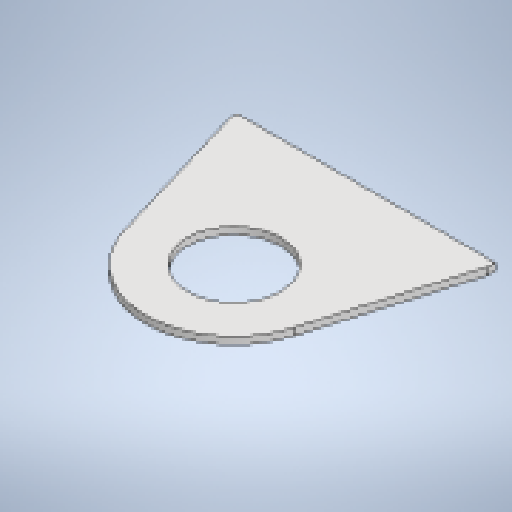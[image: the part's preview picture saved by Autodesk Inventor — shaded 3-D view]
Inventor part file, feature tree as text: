
AUTODESK INVENTOR PART (.ipt)
format: ipt  version: 2025.1 (Build 291241020, 241B)  size: 181,248 bytes
history: native  units: mm
features: other x2, sheet_metal_op x1, sketch x1
ambient origin geometry x8: Origin, YZ Plane, XZ Plane, XY Plane, X Axis, Y Axis, Z Axis, Center Point
bodies: Solid1 (feature_tree)
feature tree (4):
  sheet_metal_op  "Face1"
  sketch  "Sketch1"  dims[d0=300.0mm d1=351.020327mm d2=127.0mm d4=10.0mm d5=10.0mm d17=5.759587mm d18=240.0mm]
  other  "Plate1"
  other  "Definition1"
